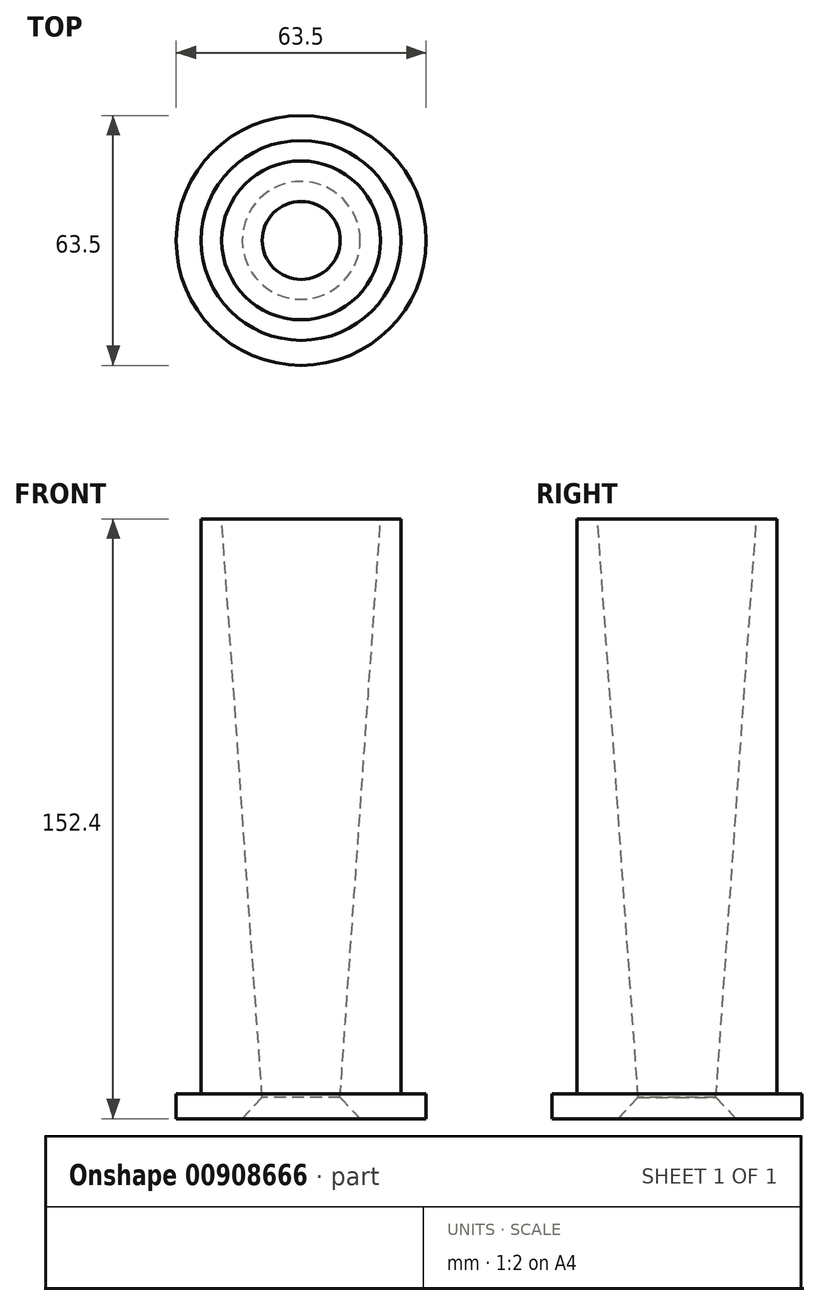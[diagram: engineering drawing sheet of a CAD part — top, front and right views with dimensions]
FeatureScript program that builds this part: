
annotation { "Feature Type Name" : "Feature", "Feature Type Description" : "" }
export const myFeature = defineFeature(function(context is Context, id is Id, definition is map)
    precondition{}
    {
        {
            var Q0;
            Q0=qCreatedBy(makeId("Top.planeOp"),FACE);
            var sketch = newSketch(context, id + "F0", { "sketchPlane" : qUnion([Q0])});
            skCircle(sketch, "E0", {"center": v(0, 0) * mm, "radius": 25.4 * mm});
            skCircle(sketch, "E1", {"center": v(0, 0) * mm, "radius": 31.75 * mm});
            skCircle(sketch, "E2", {"center": v(0, 0) * mm, "radius": 9.53 * mm});
            skSolve(sketch);
        }
        {
            var Q0;
            Q0=makeQuery(id+"F0.imprint","IMPRINT",FACE,{"disambiguationData":[TD([[makeQuery(id+"F0.imprint","IMPRINT",EDGE,{"derivedFrom":sQuery(id+"F0.wireOp",EDGE,"E0")}),-1.0]])]});
            extrude(context, id + "F1", {"entities" : qUnion([Q0]), "depth" : 6.35 * mm, "offsetDistance" : 25.4 * mm});
        }
        {
            var Q0;
            Q0=makeQuery(id+"F0.imprint","IMPRINT",FACE,{"disambiguationData":[TD([[makeQuery(id+"F0.imprint","IMPRINT",EDGE,{"derivedFrom":sQuery(id+"F0.wireOp",EDGE,"E0")}),1.0]])]});
            extrude(context, id + "F2", {"entities" : qUnion([Q0]), "operationType" : NewBodyOperationType.ADD, "depth" : 152.4 * mm, "offsetDistance" : 25.4 * mm});
        }
        {
            var Q0;
            Q0=makeQuery(id+"F0.imprint","IMPRINT",FACE,{"disambiguationData":[TD([[makeQuery(id+"F0.imprint","IMPRINT",EDGE,{"derivedFrom":sQuery(id+"F0.wireOp",EDGE,"E2")}),1.0]])]});
            extrude(context, id + "F3", {"entities" : qUnion([Q0]), "operationType" : NewBodyOperationType.REMOVE, "endBound" : BoundingType.THROUGH_ALL, "depth" : 25.4 * mm, "offsetDistance" : 25.4 * mm, "hasDraft" : true, "draftAngle" : 4 * degree});
        }
        {
            var Q0;
            {var subQ0=sQuery(id+"F0.wireOp",EDGE,"E2");Q0=makeQuery(id+"F3.boolean.opBoolean","MERGE",EDGE,{"derivedFrom":[makeQuery(id+"F2.opExtrude","CAP_EDGE",EDGE,{"disambiguationData":[OSD([subQ0])],"isStart":true})],"fromTools":[makeQuery(id+"F3.opExtrude","CAP_EDGE",EDGE,{"disambiguationData":[OSD([subQ0])],"isStart":true})]});}
            chamfer(context, id + "F4", {"entities" : qUnion([Q0]), "width" : 5.08 * mm, "tangentPropagation" : true});
        }
    });
